# Revit family: Bitpop C 1.0
name_source: partatom
category: Lighting Fixtures
revit_build: Autodesk Revit 2017 (Build: 20170419_0315(x64)
units: mm (PartAtom-declared; Revit-internal decimal feet)

## family parameters
Always vertical = No
Cut with Voids When Loaded = No
Light Source = Yes
OmniClass Number = 23.80.70.00
OmniClass Title = Lighting
Part Type = Normal
Room Calculation Point = Yes
Round Connector Dimension = Use Diameter
Shared = No
Work Plane-Based = Yes

## types (4) — shared parameters
Apparent Load Phase 1 = 7 W
Body = L&L_White aluminium
CRI = 90 (also available: CRI 80 - ref. URL Technical sheet)
Code = BC1000 B 0 White - Black; BC1000 N 0 Black - White
Color Filter = 16777215
Control system = on/off; 1-10V + PUSH; DALI + PUSH
Cutout dimensions = -
Default Elevation = 1219 mm
Delivered lumen output = 335 lm (3000K, 30°)
Description = Indoor ceiling mounted
Dimming Lamp Color Temperature Shift = <None>
Emit from Line Length = 610 mm
Energy efficiency class = A A+ A++
Features = -
Geometry = Bitpop C 1.0_mod
Height mm = 81 mm  [stored 0.265748 ft]
IP = 40
Length mm = 50 mm  [stored 0.164042 ft]
Lens = L&L_Lens
Lumen output at source = 480 lm (3000K)
Manufacturer = L&L Luce&Light
Material = body in aluminium trim in steel
Model = Bitpop C 1.0
Mounting = surface mounted (ceiling)
No. and type of led = 1 high-intensity power LED
Notes = Bitpop 1.0 recessed version
Power = 6.5W
Power cables = includes 1.5 m PVC cable FROR 2x0.50 diam. 5.00 mm
Power supply = 24Vdc
Power supply unit = not included
Tilt Angle = 90.00°
Trim = L&L_Steel
URL = https://www.lucelight.it
URL Accessories and power supply units = https://www.lucelight.it
URL Catalogue = https://www.lucelight.it
URL DXF = https://www.lucelight.it
URL Description = https://www.lucelight.it
URL General code = https://www.lucelight.it
URL IES Photometric file = https://www.lucelight.it
URL Image = https://www.lucelight.it
URL Technical sheet = https://www.lucelight.it
Voltage = 24 V
Weight kg = 0.30
Width mm = 50 mm  [stored 0.164042 ft]
Wiring = -

## per-type parameters (varying)
| type | LED Colour | Optics | Photometric Web File |
| Bitpop C 1.0_F 30° (3000K 6.5W 24Vdc) | 3000K (also available: 2700K and 4000K - ref. URL Technical sheet) | 30° | BITPOP C 1.0 F 30° [3000K 6.5W 24Vdc].IES |
| Bitpop C 1.0_L 42° (3000K 6.5W 24Vdc) | 3000K (also available: 2700K and 4000K - ref. URL Technical sheet) | 42° | BITPOP C 1.0 L 42° [3000K 6.5W 24Vdc].IES |
| Bitpop C 1.0_S 17° (3000K 6.5W 24Vdc) | 3000K (also available: 2700K and 4000K - ref. URL Technical sheet) | 17° | BITPOP C 1.0 S 17° [3000K 6.5W 24Vdc].IES |
| Bitpop C 1.0_W 17°x45° (3000K 6.5W 24Vdc) | 3000K (also available: 2700K and 4000K - ref. URL Technical sheet) | 17°x45° | BITPOP C 1.0 W 17°x45° [3000K 6.5W 24Vdc].IES |

note: [stored X ft] marks values corroborated as IEEE doubles in the binary element streams (Revit-internal decimal feet)

## geometry (parser evidence)
native form markers: Blend x2, Sweep x6
no freeform markers — native parametric forms only
